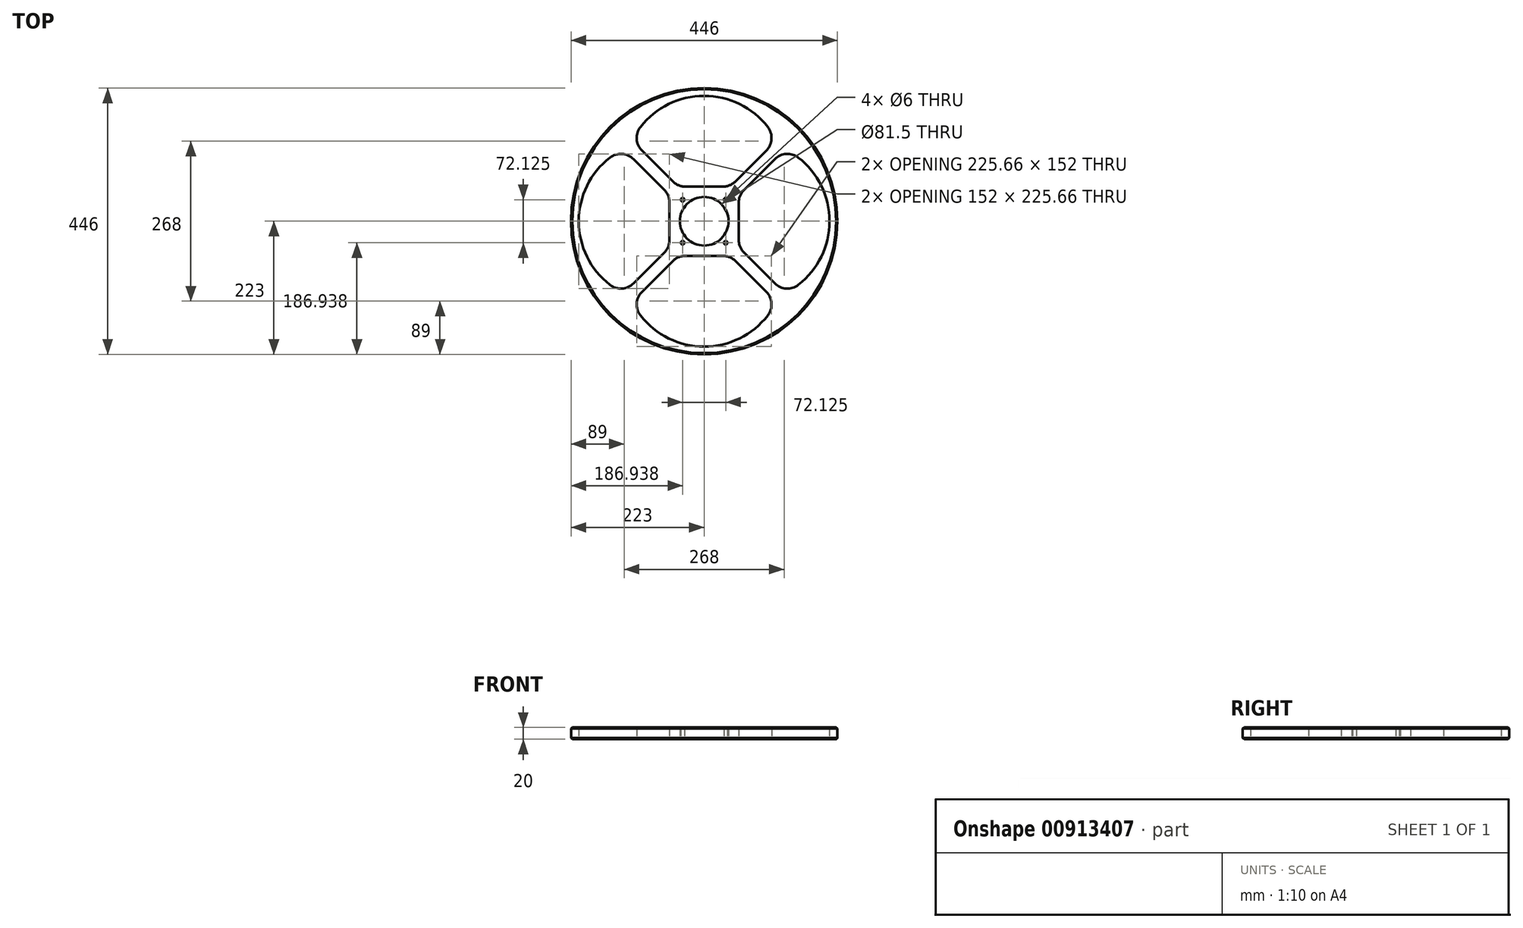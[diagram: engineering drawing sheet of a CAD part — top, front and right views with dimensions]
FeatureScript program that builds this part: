
annotation { "Feature Type Name" : "Feature", "Feature Type Description" : "" }
export const myFeature = defineFeature(function(context is Context, id is Id, definition is map)
    precondition{}
    {
        {
            var Q0;
            Q0=qCreatedBy(makeId("Top.planeOp"),FACE);
            var sketch = newSketch(context, id + "F0", { "sketchPlane" : qUnion([Q0])});
            skCircle(sketch, "E0", {"center": v(0, 0) * mm, "radius": 223 * mm});
            skCircle(sketch, "E1", {"center": v(0, 0) * mm, "radius": 40.75 * mm});
            skCircle(sketch, "E2", {"center": v(0, 0) * mm, "radius": 51 * mm, "construction": true});
            skLineSegment(sketch, "E3", {"start": v(-164.32, -164.32) * mm, "end": v(128.63, 128.63) * mm, "construction": true});
            skLineSegment(sketch, "E4", {"start": v(228.82, 0) * mm, "end": v(-253.65, 0) * mm, "construction": true});
            skCircle(sketch, "E5", {"center": v(36.06, 36.06) * mm, "radius": 3 * mm});
            skCircle(sketch, "E6.1.0", {"center": v(-36.06, 36.06) * mm, "radius": 3 * mm});
            skCircle(sketch, "E6.2.0", {"center": v(-36.06, -36.06) * mm, "radius": 3 * mm});
            skCircle(sketch, "E7.1.3.0", {"center": v(36.06, -36.06) * mm, "radius": 3 * mm});
            skLineSegment(sketch, "E8.bottom", {"start": v(-31.43, 58) * mm, "end": v(31.43, 58) * mm});
            skLineSegment(sketch, "E9", {"start": v(0, -232.9) * mm, "end": v(0, 245.85) * mm, "construction": true});
            skLineSegment(sketch, "E10.0", {"start": v(228.82, 75) * mm, "end": v(-253.65, 75) * mm, "construction": true});
            skArc(sketch, "E11.trimOffspring", {"start": v(106.57, 157.87) * mm, "mid": v(0, 210) * mm, "end": v(-106.57, 157.87) * mm});
            skLineSegment(sketch, "E12.trimOffspring", {"start": v(-52.64, 66.79) * mm, "end": v(-104.1, 118.24) * mm});
            skLineSegment(sketch, "E13.trimOffspring", {"start": v(52.64, 66.79) * mm, "end": v(104.1, 118.24) * mm});
            skPoint(sketch, "E14.visualSharp", {"position": v(120.9, 135.05) * mm});
            skArc(sketch, "E14.filletArc", {"start": v(104.1, 118.24) * mm, "mid": v(112.83, 137.6) * mm, "end": v(106.57, 157.87) * mm});
            skPoint(sketch, "E15.visualSharp", {"position": v(-120.9, 135.05) * mm});
            skArc(sketch, "E15.filletArc", {"start": v(-106.57, 157.87) * mm, "mid": v(-112.83, 137.6) * mm, "end": v(-104.1, 118.24) * mm});
            skPoint(sketch, "E16.visualSharp", {"position": v(-43.86, 58) * mm});
            skArc(sketch, "E16.filletArc", {"start": v(-52.64, 66.79) * mm, "mid": v(-42.91, 60.28) * mm, "end": v(-31.43, 58) * mm});
            skPoint(sketch, "E17.visualSharp", {"position": v(43.86, 58) * mm});
            skArc(sketch, "E17.filletArc", {"start": v(31.43, 58) * mm, "mid": v(42.91, 60.28) * mm, "end": v(52.64, 66.79) * mm});
            skArc(sketch, "E18.1.0", {"start": v(-157.87, 106.57) * mm, "mid": v(-210, 0) * mm, "end": v(-157.87, -106.57) * mm});
            skLineSegment(sketch, "E18.1.1", {"start": v(-66.79, 52.64) * mm, "end": v(-118.24, 104.1) * mm});
            skLineSegment(sketch, "E18.1.2", {"start": v(-66.79, -52.64) * mm, "end": v(-118.24, -104.1) * mm});
            skPoint(sketch, "E18.1.3", {"position": v(-135.05, -120.9) * mm});
            skPoint(sketch, "E18.1.4", {"position": v(-135.05, 120.9) * mm});
            skArc(sketch, "E18.1.5", {"start": v(-157.87, -106.57) * mm, "mid": v(-137.6, -112.83) * mm, "end": v(-118.24, -104.1) * mm});
            skPoint(sketch, "E18.1.6", {"position": v(-58, 43.86) * mm});
            skLineSegment(sketch, "E18.1.7", {"start": v(-58, -31.43) * mm, "end": v(-58, 31.43) * mm});
            skArc(sketch, "E18.1.8", {"start": v(-118.24, 104.1) * mm, "mid": v(-137.6, 112.83) * mm, "end": v(-157.87, 106.57) * mm});
            skPoint(sketch, "E18.1.9", {"position": v(-58, -43.86) * mm});
            skArc(sketch, "E18.1.10", {"start": v(-66.79, -52.64) * mm, "mid": v(-60.28, -42.91) * mm, "end": v(-58, -31.43) * mm});
            skArc(sketch, "E18.1.11", {"start": v(-58, 31.43) * mm, "mid": v(-60.28, 42.91) * mm, "end": v(-66.79, 52.64) * mm});
            skArc(sketch, "E18.2.0", {"start": v(-106.57, -157.87) * mm, "mid": v(0, -210) * mm, "end": v(106.57, -157.87) * mm});
            skLineSegment(sketch, "E18.2.1", {"start": v(-52.64, -66.79) * mm, "end": v(-104.1, -118.24) * mm});
            skLineSegment(sketch, "E18.2.2", {"start": v(52.64, -66.79) * mm, "end": v(104.1, -118.24) * mm});
            skPoint(sketch, "E18.2.3", {"position": v(120.9, -135.05) * mm});
            skPoint(sketch, "E18.2.4", {"position": v(-120.9, -135.05) * mm});
            skArc(sketch, "E18.2.5", {"start": v(106.57, -157.87) * mm, "mid": v(112.83, -137.6) * mm, "end": v(104.1, -118.24) * mm});
            skPoint(sketch, "E18.2.6", {"position": v(-43.86, -58) * mm});
            skLineSegment(sketch, "E18.2.7", {"start": v(31.43, -58) * mm, "end": v(-31.43, -58) * mm});
            skArc(sketch, "E18.2.8", {"start": v(-104.1, -118.24) * mm, "mid": v(-112.83, -137.6) * mm, "end": v(-106.57, -157.87) * mm});
            skPoint(sketch, "E18.2.9", {"position": v(43.86, -58) * mm});
            skArc(sketch, "E18.2.10", {"start": v(52.64, -66.79) * mm, "mid": v(42.91, -60.28) * mm, "end": v(31.43, -58) * mm});
            skArc(sketch, "E18.2.11", {"start": v(-31.43, -58) * mm, "mid": v(-42.91, -60.28) * mm, "end": v(-52.64, -66.79) * mm});
            skArc(sketch, "E18.3.0", {"start": v(157.87, -106.57) * mm, "mid": v(210, 0) * mm, "end": v(157.87, 106.57) * mm});
            skLineSegment(sketch, "E18.3.1", {"start": v(66.79, -52.64) * mm, "end": v(118.24, -104.1) * mm});
            skLineSegment(sketch, "E18.3.2", {"start": v(66.79, 52.64) * mm, "end": v(118.24, 104.1) * mm});
            skPoint(sketch, "E18.3.3", {"position": v(135.05, 120.9) * mm});
            skPoint(sketch, "E18.3.4", {"position": v(135.05, -120.9) * mm});
            skArc(sketch, "E18.3.5", {"start": v(157.87, 106.57) * mm, "mid": v(137.6, 112.83) * mm, "end": v(118.24, 104.1) * mm});
            skPoint(sketch, "E18.3.6", {"position": v(58, -43.86) * mm});
            skLineSegment(sketch, "E18.3.7", {"start": v(58, 31.43) * mm, "end": v(58, -31.43) * mm});
            skArc(sketch, "E18.3.8", {"start": v(118.24, -104.1) * mm, "mid": v(137.6, -112.83) * mm, "end": v(157.87, -106.57) * mm});
            skPoint(sketch, "E18.3.9", {"position": v(58, 43.86) * mm});
            skArc(sketch, "E18.3.10", {"start": v(66.79, 52.64) * mm, "mid": v(60.28, 42.91) * mm, "end": v(58, 31.43) * mm});
            skArc(sketch, "E18.3.11", {"start": v(58, -31.43) * mm, "mid": v(60.28, -42.91) * mm, "end": v(66.79, -52.64) * mm});
            skSolve(sketch);
        }
        {
            var Q0;
            Q0=makeQuery(id+"F0.imprint","IMPRINT",FACE,{"disambiguationData":[TD([[makeQuery(id+"F0.imprint","IMPRINT",EDGE,{"derivedFrom":sQuery(id+"F0.wireOp",EDGE,"E0")}),1.0]])]});
            extrude(context, id + "F1", {"entities" : qUnion([Q0]), "depth" : 20 * mm, "offsetDistance" : 25 * mm});
        }
        {
            var Q0;
            Q0=makeQuery(id+"F1.opExtrude","CAP_EDGE",EDGE,{"disambiguationData":[OSD([sQuery(id+"F0.wireOp",EDGE,"E0")])],"isStart":true});
            var Q1;
            Q1=makeQuery(id+"F1.opExtrude","CAP_EDGE",EDGE,{"disambiguationData":[OSD([sQuery(id+"F0.wireOp",EDGE,"E0")])],"isStart":false});
            chamfer(context, id + "F2", {"entities" : qUnion([Q0, Q1]), "width" : 2 * mm, "tangentPropagation" : true});
        }
    });
